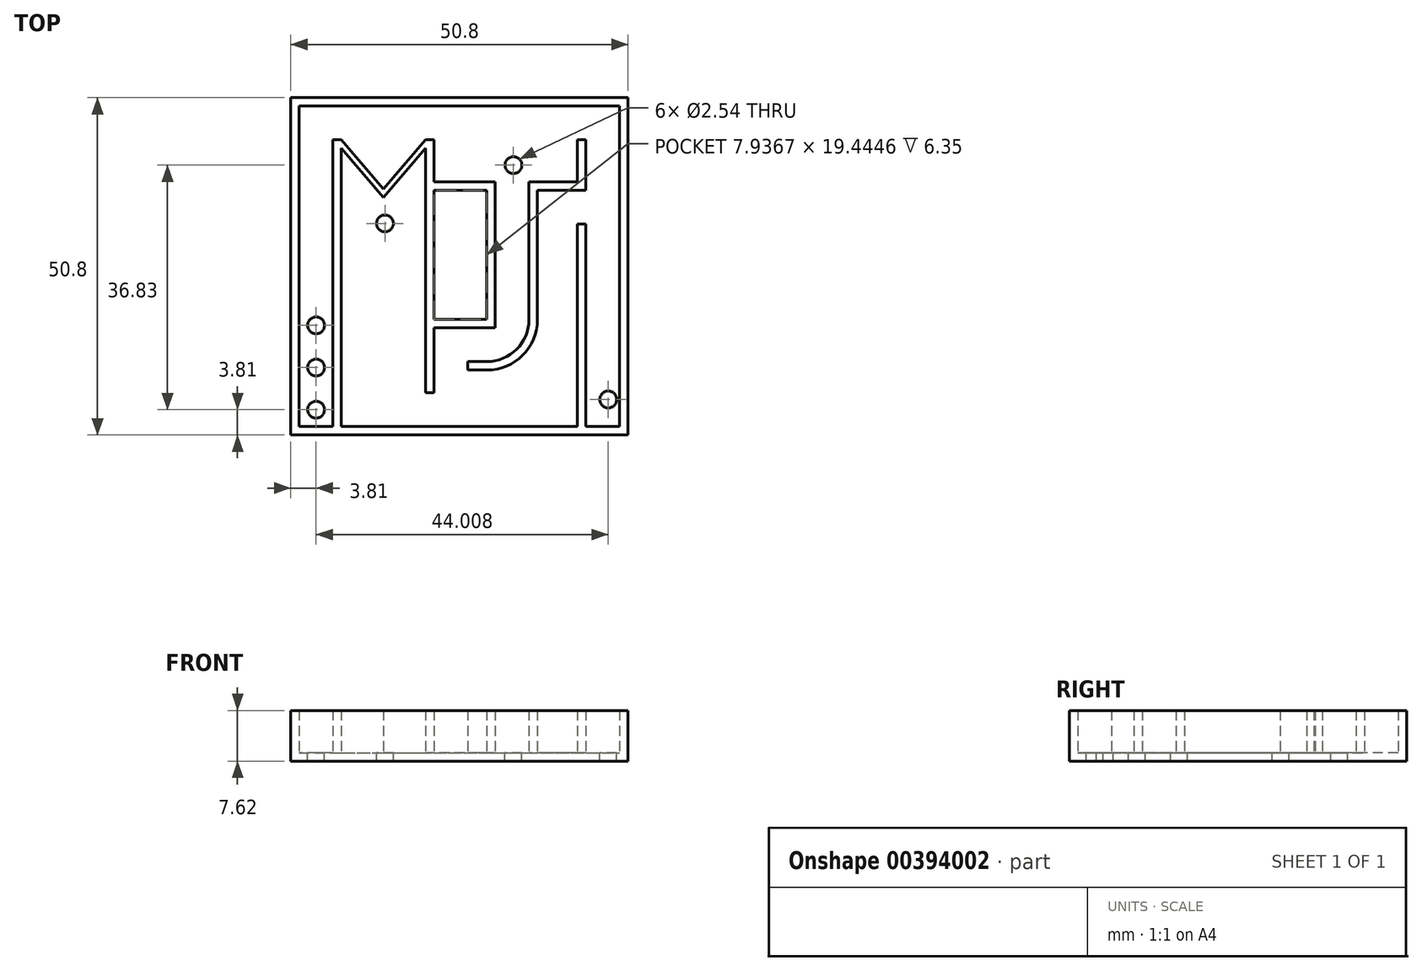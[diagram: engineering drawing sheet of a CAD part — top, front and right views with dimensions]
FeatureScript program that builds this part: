
annotation { "Feature Type Name" : "Feature", "Feature Type Description" : "" }
export const myFeature = defineFeature(function(context is Context, id is Id, definition is map)
    precondition{}
    {
        {
            var Q0;
            Q0=qCreatedBy(makeId("Top.planeOp"),FACE);
            var sketch = newSketch(context, id + "F0", { "sketchPlane" : qUnion([Q0])});
            skLineSegment(sketch, "E0", {"start": v(0, 50.8) * mm, "end": v(50.8, 50.8) * mm});
            skLineSegment(sketch, "E1", {"start": v(50.8, 50.8) * mm, "end": v(50.8, 0) * mm});
            skLineSegment(sketch, "E2", {"start": v(50.8, 0) * mm, "end": v(0, 0) * mm});
            skLineSegment(sketch, "E3", {"start": v(0, 0) * mm, "end": v(0, 50.8) * mm});
            skSolve(sketch);
        }
        {
            var Q0;
            Q0=makeQuery(id+"F0.imprint","IMPRINT",FACE,{"disambiguationData":[TD([[makeQuery(id+"F0.imprint","IMPRINT",EDGE,{"derivedFrom":sQuery(id+"F0.wireOp",EDGE,"E0")}),-1.0]])]});
            extrude(context, id + "F1", {"entities" : qUnion([Q0]), "depth" : 7.62 * mm});
        }
        {
            var Q0;
            Q0=makeQuery(id+"F1.opExtrude","CAP_FACE",FACE,{"disambiguationData":[OSD([sQuery(id+"F0.wireOp",EDGE,"E0"),sQuery(id+"F0.wireOp",EDGE,"E1"),sQuery(id+"F0.wireOp",EDGE,"E2"),sQuery(id+"F0.wireOp",EDGE,"E3")])],"isStart":false});
            shell(context, id + "F2", {"entities" : qUnion([Q0]), "thickness" : 1.27 * mm});
        }
        {
            var Q0;
            Q0=makeQuery(id+"F2.opShell","OFFSET_FACE",FACE,{"disambiguationData":[OSD([sQuery(id+"F0.wireOp",EDGE,"E0"),sQuery(id+"F0.wireOp",EDGE,"E1"),sQuery(id+"F0.wireOp",EDGE,"E2"),sQuery(id+"F0.wireOp",EDGE,"E3")])]});
            var sketch = newSketch(context, id + "F3", { "sketchPlane" : qUnion([Q0])});
            skLineSegment(sketch, "E4", {"start": v(6.35, 1.27) * mm, "end": v(6.35, 44.45) * mm});
            skLineSegment(sketch, "E5", {"start": v(6.35, 44.45) * mm, "end": v(7.62, 44.45) * mm});
            skLineSegment(sketch, "E6", {"start": v(7.62, 44.45) * mm, "end": v(7.62, 1.27) * mm});
            skLineSegment(sketch, "E7", {"start": v(7.62, 1.27) * mm, "end": v(6.35, 1.27) * mm});
            skCircle(sketch, "E8", {"center": v(3.81, 3.81) * mm, "radius": 1.27 * mm});
            skSolve(sketch);
        }
        {
            var Q0;
            Q0=makeQuery(id+"F3.imprint","IMPRINT",FACE,{"disambiguationData":[TD([[makeQuery(id+"F3.imprint","IMPRINT",EDGE,{"derivedFrom":sQuery(id+"F3.wireOp",EDGE,"E8")}),1.0]])]});
            extrude(context, id + "F4", {"entities" : qUnion([Q0]), "operationType" : NewBodyOperationType.REMOVE, "oppositeDirection" : true, "depth" : 12.7 * mm});
        }
        {
            var Q0;
            Q0=makeQuery(id+"F2.opShell","OFFSET_FACE",FACE,{"disambiguationData":[OSD([sQuery(id+"F0.wireOp",EDGE,"E0"),sQuery(id+"F0.wireOp",EDGE,"E1"),sQuery(id+"F0.wireOp",EDGE,"E2"),sQuery(id+"F0.wireOp",EDGE,"E3")])]});
            var sketch = newSketch(context, id + "F5", { "sketchPlane" : qUnion([Q0])});
            skLineSegment(sketch, "E9.bottom", {"start": v(6.35, 1.27) * mm, "end": v(7.62, 1.27) * mm});
            skLineSegment(sketch, "E9.top", {"start": v(6.35, 44.45) * mm, "end": v(7.62, 44.45) * mm});
            skLineSegment(sketch, "E9.left", {"start": v(6.35, 1.27) * mm, "end": v(6.35, 44.45) * mm});
            skLineSegment(sketch, "E9.right", {"start": v(7.62, 1.27) * mm, "end": v(7.62, 44.45) * mm});
            skSolve(sketch);
        }
        {
            var Q0;
            Q0=makeQuery(id+"F5.imprint","IMPRINT",FACE,{"disambiguationData":[TD([[makeQuery(id+"F5.imprint","IMPRINT",EDGE,{"derivedFrom":sQuery(id+"F5.wireOp",EDGE,"E9.bottom")}),-1.0]])]});
            extrude(context, id + "F6", {"entities" : qUnion([Q0]), "operationType" : NewBodyOperationType.ADD, "depth" : 6.35 * mm});
        }
        {
            var Q0;
            Q0=makeQuery(id+"F2.opShell","OFFSET_FACE",FACE,{"disambiguationData":[OSD([sQuery(id+"F0.wireOp",EDGE,"E0"),sQuery(id+"F0.wireOp",EDGE,"E1"),sQuery(id+"F0.wireOp",EDGE,"E2"),sQuery(id+"F0.wireOp",EDGE,"E3")])]});
            var sketch = newSketch(context, id + "F7", { "sketchPlane" : qUnion([Q0])});
            skLineSegment(sketch, "E10", {"start": v(20.32, 44.45) * mm, "end": v(20.32, 6.35) * mm});
            skLineSegment(sketch, "E11", {"start": v(20.32, 6.35) * mm, "end": v(21.59, 6.35) * mm});
            skLineSegment(sketch, "E12", {"start": v(21.59, 6.35) * mm, "end": v(21.59, 44.45) * mm});
            skLineSegment(sketch, "E13", {"start": v(21.59, 44.45) * mm, "end": v(20.32, 44.45) * mm});
            skLineSegment(sketch, "E14", {"start": v(7.62, 44.45) * mm, "end": v(13.97, 37.04) * mm});
            skLineSegment(sketch, "E15", {"start": v(13.97, 37.04) * mm, "end": v(20.32, 44.45) * mm});
            skLineSegment(sketch, "E16", {"start": v(7.62, 43.18) * mm, "end": v(13.97, 35.77) * mm});
            skLineSegment(sketch, "E17", {"start": v(13.97, 35.77) * mm, "end": v(20.32, 43.18) * mm});
            skLineSegment(sketch, "E18", {"start": v(20.32, 43.18) * mm, "end": v(20.32, 44.45) * mm});
            skLineSegment(sketch, "E19", {"start": v(7.62, 43.18) * mm, "end": v(7.62, 44.45) * mm});
            skSolve(sketch);
        }
        {
            var Q0;
            Q0=makeQuery(id+"F7.imprint","IMPRINT",FACE,{"disambiguationData":[TD([[makeQuery(id+"F7.imprint","IMPRINT",EDGE,{"derivedFrom":sQuery(id+"F7.wireOp",EDGE,"E10")}),-1.0]])]});
            var sketch = newSketch(context, id + "F8", { "sketchPlane" : qUnion([Q0])});
            skLineSegment(sketch, "E20", {"start": v(21.59, 44.45) * mm, "end": v(44.45, 44.45) * mm});
            skLineSegment(sketch, "E21", {"start": v(44.45, 44.45) * mm, "end": v(44.45, 38.1) * mm});
            skLineSegment(sketch, "E22", {"start": v(44.45, 38.1) * mm, "end": v(35.88, 38.1) * mm});
            skLineSegment(sketch, "E23", {"start": v(35.88, 38.1) * mm, "end": v(35.88, 17.39) * mm});
            skLineSegment(sketch, "E24", {"start": v(29.53, 11.04) * mm, "end": v(26.67, 11.04) * mm});
            skLineSegment(sketch, "E25", {"start": v(26.67, 11.04) * mm, "end": v(26.67, 16.12) * mm});
            skLineSegment(sketch, "E26", {"start": v(26.67, 16.12) * mm, "end": v(30.8, 16.12) * mm});
            skLineSegment(sketch, "E27", {"start": v(30.8, 16.12) * mm, "end": v(30.8, 38.1) * mm});
            skLineSegment(sketch, "E28", {"start": v(30.8, 38.1) * mm, "end": v(21.59, 38.1) * mm});
            skLineSegment(sketch, "E29", {"start": v(21.59, 38.1) * mm, "end": v(21.59, 44.45) * mm});
            skPoint(sketch, "E30.visualSharp", {"position": v(35.88, 11.04) * mm});
            skArc(sketch, "E30.filletArc", {"start": v(29.53, 11.04) * mm, "mid": v(34.02, 12.9) * mm, "end": v(35.88, 17.39) * mm});
            skLineSegment(sketch, "E31.0", {"start": v(21.59, 6.35) * mm, "end": v(21.59, 44.45) * mm});
            skLineSegment(sketch, "E32", {"start": v(21.59, 44.45) * mm, "end": v(21.59, 43.18) * mm});
            skLineSegment(sketch, "E33", {"start": v(21.59, 43.18) * mm, "end": v(44.45, 43.18) * mm});
            skLineSegment(sketch, "E34.0", {"start": v(43.18, 44.45) * mm, "end": v(43.18, 38.1) * mm});
            skLineSegment(sketch, "E35.0", {"start": v(44.45, 36.83) * mm, "end": v(35.88, 36.83) * mm});
            skLineSegment(sketch, "E36", {"start": v(44.45, 36.83) * mm, "end": v(44.45, 38.1) * mm});
            skLineSegment(sketch, "E37.0", {"start": v(37.15, 37.85) * mm, "end": v(37.15, 17.39) * mm});
            skLineSegment(sketch, "E38.0", {"start": v(30.96, 36.83) * mm, "end": v(21.59, 36.83) * mm});
            skLineSegment(sketch, "E39.0", {"start": v(29.53, 16.12) * mm, "end": v(29.53, 38.35) * mm});
            skLineSegment(sketch, "E40.0", {"start": v(26.67, 17.39) * mm, "end": v(30.96, 17.39) * mm});
            skArc(sketch, "E41.0", {"start": v(29.53, 9.77) * mm, "mid": v(34.91, 12) * mm, "end": v(37.15, 17.39) * mm});
            skLineSegment(sketch, "E42.0", {"start": v(29.53, 9.77) * mm, "end": v(26.67, 9.77) * mm});
            skLineSegment(sketch, "E43", {"start": v(26.67, 9.77) * mm, "end": v(26.67, 11.04) * mm});
            skLineSegment(sketch, "E44", {"start": v(26.67, 16.12) * mm, "end": v(26.67, 17.39) * mm});
            skLineSegment(sketch, "E45", {"start": v(26.67, 16.12) * mm, "end": v(21.59, 16.12) * mm});
            skLineSegment(sketch, "E46", {"start": v(21.59, 16.12) * mm, "end": v(21.59, 17.39) * mm});
            skLineSegment(sketch, "E47", {"start": v(21.59, 17.39) * mm, "end": v(26.67, 17.39) * mm});
            skSolve(sketch);
        }
        {
            var Q0;
            {var subQ0=sQuery(id+"F8.wireOp",EDGE,"E32");Q0=makeQuery(id+"F8.imprint","IMPRINT",FACE,{"disambiguationData":[TD([[makeQuery(id+"F8.imprint","IMPRINT",EDGE,{"derivedFrom":subQ0}),-1.0]])]});}
            var Q1;
            {var subQ0=sQuery(id+"F8.wireOp",EDGE,"E21");var subQ1=sQuery(id+"F8.wireOp",EDGE,"E20");var subQ2=makeQuery(id+"F8.imprint","INTERSECT",VERTEX,{"derivedFrom":[subQ1,subQ0]});Q1=makeQuery(id+"F8.imprint","IMPRINT",FACE,{"disambiguationData":[TD([[makeQuery(id+"F8.imprint","IMPRINT",EDGE,{"disambiguationData":[TD([[subQ2,1.0]])],"derivedFrom":subQ1}),-1.0]])]});}
            var Q2;
            {var subQ1=sQuery(id+"F8.wireOp",EDGE,"E21");var subQ3=sQuery(id+"F8.wireOp",EDGE,"E33");var subQ4=makeQuery(id+"F8.imprint","INTERSECT",VERTEX,{"derivedFrom":[subQ1,subQ3]});Q2=makeQuery(id+"F8.imprint","IMPRINT",FACE,{"disambiguationData":[TD([[makeQuery(id+"F8.imprint","IMPRINT",EDGE,{"disambiguationData":[TD([[subQ4,1.0]])],"derivedFrom":subQ3}),-1.0]])]});}
            var Q3;
            {var subQ0=sQuery(id+"F8.wireOp",EDGE,"E31.0");var subQ1=sQuery(id+"F8.wireOp",EDGE,"E28");var subQ2=makeQuery(id+"F8.imprint","INTERSECT",VERTEX,{"derivedFrom":[subQ1,subQ0]});Q3=makeQuery(id+"F8.imprint","IMPRINT",FACE,{"disambiguationData":[TD([[makeQuery(id+"F8.imprint","IMPRINT",EDGE,{"disambiguationData":[TD([[subQ2,1.0]])],"derivedFrom":subQ1}),1.0]])]});}
            var Q4;
            {var subQ0=sQuery(id+"F8.wireOp",EDGE,"E28");var subQ1=sQuery(id+"F8.wireOp",EDGE,"E27");var subQ2=makeQuery(id+"F8.imprint","INTERSECT",VERTEX,{"derivedFrom":[subQ1,subQ0]});Q4=makeQuery(id+"F8.imprint","IMPRINT",FACE,{"disambiguationData":[TD([[makeQuery(id+"F8.imprint","IMPRINT",EDGE,{"disambiguationData":[TD([[subQ2,1.0]])],"derivedFrom":subQ1}),1.0]])]});}
            var Q5;
            {var subQ0=sQuery(id+"F8.wireOp",EDGE,"E40.0");var subQ1=sQuery(id+"F8.wireOp",EDGE,"E27");var subQ2=makeQuery(id+"F8.imprint","INTERSECT",VERTEX,{"derivedFrom":[subQ1,subQ0]});Q5=makeQuery(id+"F8.imprint","IMPRINT",FACE,{"disambiguationData":[TD([[makeQuery(id+"F8.imprint","IMPRINT",EDGE,{"disambiguationData":[TD([[subQ2,-1.0]])],"derivedFrom":subQ1}),1.0]])]});}
            var Q6;
            {var subQ0=sQuery(id+"F8.wireOp",EDGE,"E44");Q6=makeQuery(id+"F8.imprint","IMPRINT",FACE,{"disambiguationData":[TD([[makeQuery(id+"F8.imprint","IMPRINT",EDGE,{"derivedFrom":subQ0}),-1.0]])]});}
            var Q7;
            {var subQ0=sQuery(id+"F8.wireOp",EDGE,"E27");var subQ1=sQuery(id+"F8.wireOp",EDGE,"E26");var subQ2=makeQuery(id+"F8.imprint","INTERSECT",VERTEX,{"derivedFrom":[subQ1,subQ0]});Q7=makeQuery(id+"F8.imprint","IMPRINT",FACE,{"disambiguationData":[TD([[makeQuery(id+"F8.imprint","IMPRINT",EDGE,{"disambiguationData":[TD([[subQ2,1.0]])],"derivedFrom":subQ1}),1.0]])]});}
            var Q8;
            Q8=makeQuery(id+"F8.imprint","IMPRINT",FACE,{"disambiguationData":[TD([[makeQuery(id+"F8.imprint","IMPRINT",EDGE,{"derivedFrom":sQuery(id+"F8.wireOp",EDGE,"E44")}),1.0]])]});
            var Q9;
            Q9=makeQuery(id+"F8.imprint","IMPRINT",FACE,{"disambiguationData":[TD([[makeQuery(id+"F8.imprint","IMPRINT",EDGE,{"derivedFrom":sQuery(id+"F8.wireOp",EDGE,"E24")}),1.0]])]});
            var Q10;
            {var subQ0=sQuery(id+"F8.wireOp",EDGE,"E36");Q10=makeQuery(id+"F8.imprint","IMPRINT",FACE,{"disambiguationData":[TD([[makeQuery(id+"F8.imprint","IMPRINT",EDGE,{"derivedFrom":subQ0}),1.0]])]});}
            extrude(context, id + "F9", {"entities" : qUnion([Q0, Q1, Q2, Q3, Q4, Q5, Q6, Q7, Q8, Q9, Q10]), "operationType" : NewBodyOperationType.ADD, "depth" : 6.35 * mm});
        }
        {
            var Q0;
            Q0=makeQuery(id+"F7.imprint","IMPRINT",FACE,{"disambiguationData":[TD([[makeQuery(id+"F7.imprint","IMPRINT",EDGE,{"derivedFrom":sQuery(id+"F7.wireOp",EDGE,"E14")}),-1.0]])]});
            var Q1;
            Q1=makeQuery(id+"F7.imprint","IMPRINT",FACE,{"disambiguationData":[TD([[makeQuery(id+"F7.imprint","IMPRINT",EDGE,{"derivedFrom":sQuery(id+"F7.wireOp",EDGE,"E10")}),1.0]])]});
            extrude(context, id + "F10", {"entities" : qUnion([Q0, Q1]), "operationType" : NewBodyOperationType.ADD, "depth" : 6.35 * mm});
        }
        {
            var Q0;
            Q0=makeQuery(id+"F7.imprint","IMPRINT",FACE,{"disambiguationData":[TD([[makeQuery(id+"F7.imprint","IMPRINT",EDGE,{"derivedFrom":sQuery(id+"F7.wireOp",EDGE,"E10")}),-1.0]])]});
            var sketch = newSketch(context, id + "F11", { "sketchPlane" : qUnion([Q0])});
            skLineSegment(sketch, "E48", {"start": v(44.45, 1.28) * mm, "end": v(44.45, 31.75) * mm});
            skLineSegment(sketch, "E49", {"start": v(44.45, 31.75) * mm, "end": v(43.18, 31.75) * mm});
            skLineSegment(sketch, "E50", {"start": v(43.18, 31.75) * mm, "end": v(43.18, 1.28) * mm});
            skLineSegment(sketch, "E51", {"start": v(43.18, 1.28) * mm, "end": v(44.45, 1.28) * mm});
            skSolve(sketch);
        }
        {
            var Q0;
            Q0 = qSketchRegion(id + "F11", true);
            extrude(context, id + "F12", {"entities" : qUnion([Q0]), "operationType" : NewBodyOperationType.ADD, "depth" : 6.35 * mm});
        }
        {
            var Q0;
            Q0=makeQuery(id+"F7.imprint","IMPRINT",FACE,{"disambiguationData":[TD([[makeQuery(id+"F7.imprint","IMPRINT",EDGE,{"derivedFrom":sQuery(id+"F7.wireOp",EDGE,"E10")}),-1.0]])]});
            var sketch = newSketch(context, id + "F13", { "sketchPlane" : qUnion([Q0])});
            skCircle(sketch, "E52", {"center": v(3.81, 10.16) * mm, "radius": 1.27 * mm});
            skCircle(sketch, "E53", {"center": v(3.8, 16.51) * mm, "radius": 1.27 * mm});
            skCircle(sketch, "E54", {"center": v(14.18, 31.85) * mm, "radius": 1.27 * mm});
            skCircle(sketch, "E55", {"center": v(33.53, 40.64) * mm, "radius": 1.27 * mm});
            skCircle(sketch, "E56", {"center": v(47.82, 5.34) * mm, "radius": 1.27 * mm});
            skSolve(sketch);
        }
        {
            var Q0;
            Q0 = qSketchRegion(id + "F13", true);
            extrude(context, id + "F14", {"entities" : qUnion([Q0]), "operationType" : NewBodyOperationType.REMOVE, "oppositeDirection" : true, "depth" : 12.7 * mm});
        }
    });
